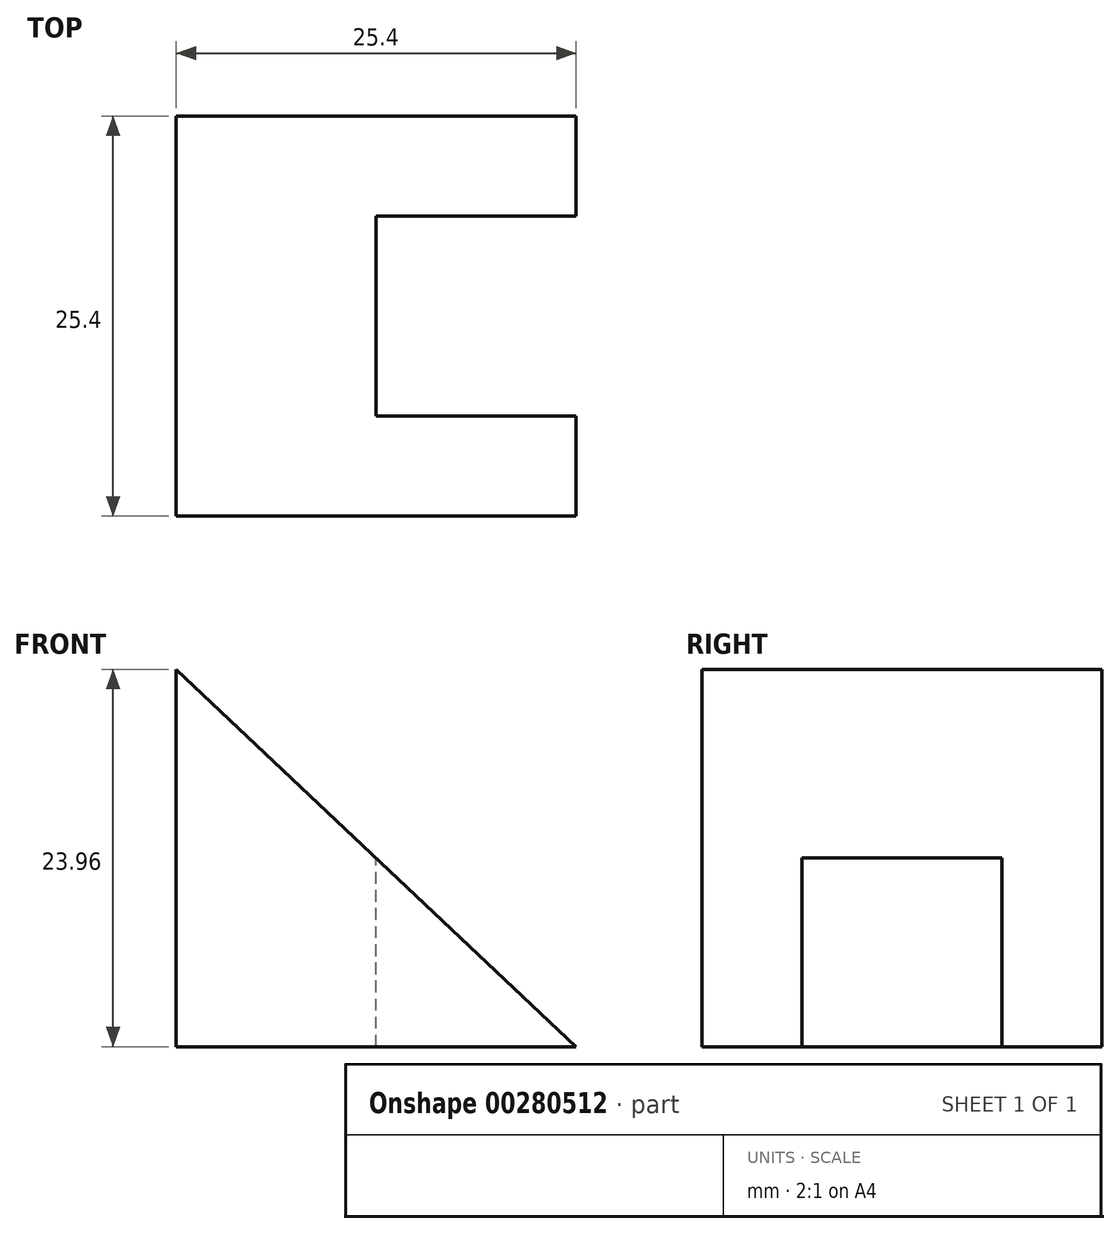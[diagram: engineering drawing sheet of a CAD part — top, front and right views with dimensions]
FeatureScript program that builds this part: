
annotation { "Feature Type Name" : "Feature", "Feature Type Description" : "" }
export const myFeature = defineFeature(function(context is Context, id is Id, definition is map)
    precondition{}
    {
        {
            var Q0;
            Q0=qCreatedBy(makeId("Front.planeOp"),FACE);
            var sketch = newSketch(context, id + "F0", { "sketchPlane" : qUnion([Q0])});
            skLineSegment(sketch, "E0", {"start": v(0, 0) * mm, "end": v(25.4, 0) * mm});
            skLineSegment(sketch, "E1", {"start": v(0, 0) * mm, "end": v(0, 23.96) * mm});
            skLineSegment(sketch, "E2", {"start": v(0, 23.96) * mm, "end": v(25.4, 0) * mm});
            skSolve(sketch);
        }
        {
            var Q0;
            Q0=makeQuery(id+"F0.imprint","IMPRINT",FACE,{"disambiguationData":[TD([[makeQuery(id+"F0.imprint","IMPRINT",EDGE,{"derivedFrom":sQuery(id+"F0.wireOp",EDGE,"E0")}),1.0]])]});
            extrude(context, id + "F1", {"entities" : qUnion([Q0]), "depth" : 25.4 * mm});
        }
        {
            var Q0;
            Q0=makeQuery(id+"F1.opExtrude","CAP_FACE",FACE,{"disambiguationData":[OSD([sQuery(id+"F0.wireOp",EDGE,"E0"),sQuery(id+"F0.wireOp",EDGE,"E1"),sQuery(id+"F0.wireOp",EDGE,"E2")])],"isStart":false});
            var sketch = newSketch(context, id + "F2", { "sketchPlane" : qUnion([Q0])});
            skLineSegment(sketch, "E3", {"start": v(12.7, 11.98) * mm, "end": v(25.4, 0) * mm});
            skLineSegment(sketch, "E4", {"start": v(25.4, 0) * mm, "end": v(12.7, 0) * mm});
            skLineSegment(sketch, "E5", {"start": v(12.7, 0) * mm, "end": v(12.7, 11.98) * mm});
            skSolve(sketch);
        }
        {
            var Q0;
            Q0=makeQuery(id+"F2.imprint","IMPRINT",FACE,{"disambiguationData":[TD([[makeQuery(id+"F2.imprint","IMPRINT",EDGE,{"derivedFrom":sQuery(id+"F2.wireOp",EDGE,"E3")}),-1.0]])]});
            extrude(context, id + "F3", {"entities" : qUnion([Q0]), "operationType" : NewBodyOperationType.REMOVE, "oppositeDirection" : true, "depth" : 19.05 * mm, "hasSecondDirection" : true, "secondDirectionOppositeDirection" : true, "secondDirectionDepth" : 6.35 * mm});
        }
    });
